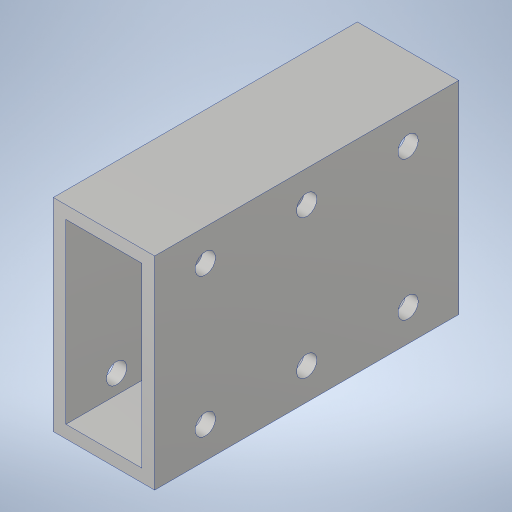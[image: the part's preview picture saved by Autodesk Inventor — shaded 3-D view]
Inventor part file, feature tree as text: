
AUTODESK INVENTOR PART (.ipt)
format: ipt  version: 2023.4 (Build 274418000, 418)  size: 238,592 bytes
history: native  units: in
note: dims shown in document units (in); Inventor stores cm internally (conversion verified against a paired STEP export)
features: extrude x1, hole x1, sketch x1, projected_geometry x1
ambient origin geometry x8: Origin, YZ Plane, XZ Plane, XY Plane, X Axis, Y Axis, Z Axis, Center Point
bodies: Solid1 (feature_tree)
feature tree (4):
  extrude  "Extrusion1"  Depth=1.0in
  hole  "Hole1"  [1 undecoded]
  sketch  "Sketch2"  dims[d4=0.0in d5=0.375in d6=0.375in d7=0.5in d8=3.937in d10=1.0in d11=0.3937in d13=1.0in d15=0.201in d16=0.75in d17=0.385in d18=0.25in d19=0.5635in d20=1.0in d21=0.8108in]
  projected_geometry  "Projected Loop1"
note: 1 required parameter value undecoded (feature->parameter linkage not recoverable at this tier; creation-order binding heuristic only, values carry confidence <= 0.55)
